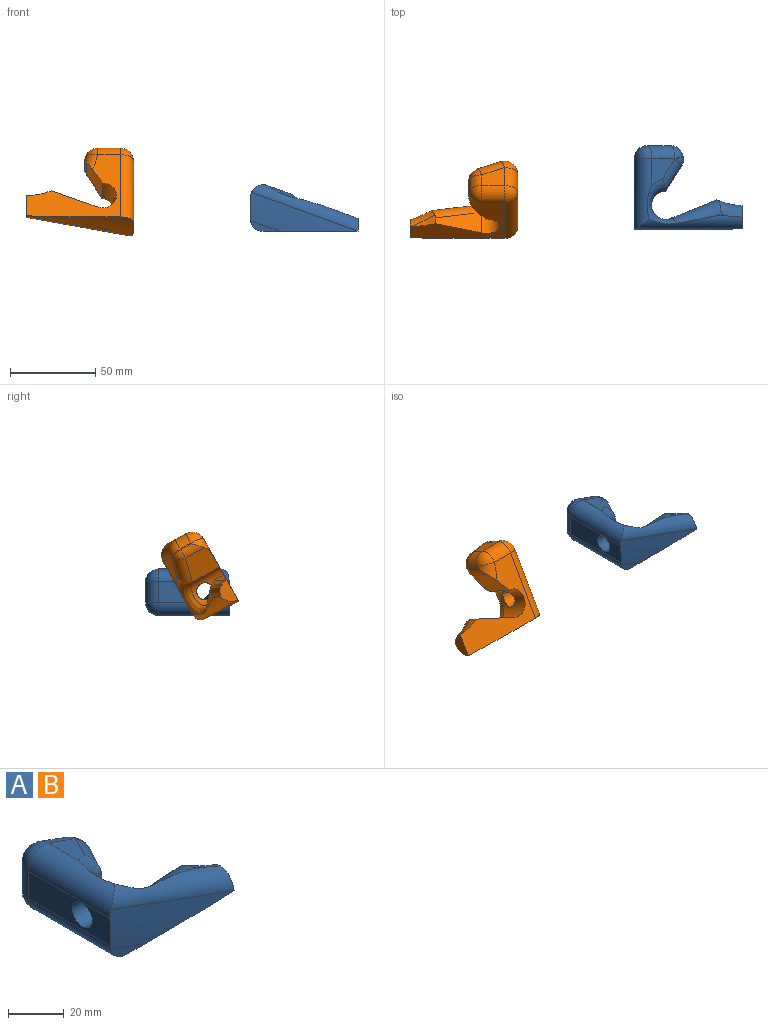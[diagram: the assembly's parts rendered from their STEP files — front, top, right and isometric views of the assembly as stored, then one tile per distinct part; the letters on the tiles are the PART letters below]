
ASSEMBLY  parts=2 mates=2
PART A: 33 faces, bbox 71.2x51.8x45.1 mm
  f0: plane 6.02x2.19mm, normal (0.34,0,0.94), area 3.4mm2, adj f30,f31,f32
  f1: plane 15.57x13.56mm, normal (0.34,0,0.94), area 138.2mm2, adj f21,f24,f27,f28,f29
  f2: plane 14.53x8.49mm, normal (1,0,0), area 77.7mm2, adj f3,f13,f31,f32
  f3: plane 55.6x41.91mm, normal (0,0,-1), area 972.8mm2, adj f2,f5,f6,f7,f8,f9,f13,f15
  f4: plane 41.86x12.11mm, normal (-1,0,0), area 424.4mm2, adj f12,f13,f15,f23,f28
  f5: plane 17.37x6.32mm, normal (0,-1,0), area 43.2mm2, adj f3,f13,f15
  f6: cylinder r=35.16mm len=13.75mm, axis (0,0,-1), area 43mm2, adj f3,f7,f30,f31
  f7: plane 26.86x13.66mm, normal (-0.37,0.93,0), area 254mm2, adj f3,f6,f8,f30
  f8: cylinder r=8.32mm len=21.65mm, axis (0,0,-1), area 472.5mm2, adj f3,f7,f9,f12,f29
  f9: plane 18.21x14.52mm, normal (0.84,-0.54,0), area 277.7mm2, adj f3,f8,f18,f22,f27,f29
  f10: cylinder r=35.16mm len=7.21mm, axis (0,0,-1), area 3.2mm2, adj f17,f18,f21,f22
  f11: plane 13.46x12.11mm, normal (0,1,0), area 130mm2, adj f16,f17,f23,f24
  f12: cylinder r=5.07mm len=10.14mm, axis (-1,0,0), area 319.1mm2, adj f4,f8
  f13: cylinder r=177.8mm len=67.98mm, axis (-0.94,0,0.34), area 685.5mm2, adj f2,f3,f4,f5,f15,f28,f32
  f14: sphere r=7.62mm, area 51.4mm2, adj f16,f17,f18
  f15: cylinder r=7.62mm len=41.87mm, axis (0,-1,0), area 501.1mm2, adj f3,f4,f5,f13,f19
  f16: cylinder r=7.62mm len=13.46mm, axis (-1,0,0), area 161.1mm2, adj f3,f11,f14,f19
  f17: cylinder r=7.62mm len=7.5mm, axis (0,0,-1), area 76.5mm2, adj f10,f11,f14,f20
  f18: torus R=42.78mm, axis (0,0,1), area 65.5mm2, adj f3,f9,f10,f14,f22
  f19: sphere r=7.62mm, area 124.4mm2, adj f15,f16,f23
  f20: sphere r=7.62mm, area 41.6mm2, adj f17,f21,f24
  f21: bspline ~7.2x4.97mm, area 4.6mm2, adj f1,f10,f20,f25
  f22: cylinder r=7.62mm len=12.8mm, axis (0,0,-1), area 58mm2, adj f9,f10,f18,f25
  f23: cylinder r=7.62mm len=12.11mm, axis (0,0,-1), area 145mm2, adj f4,f11,f19,f26
  f24: cylinder r=7.62mm len=16.06mm, axis (0.94,0,-0.34), area 171.4mm2, adj f1,f11,f20,f26
  f25: sphere r=7.62mm, area 23.8mm2, adj f21,f22,f27
  f26: sphere r=7.62mm, area 111.5mm2, adj f23,f24,f28
  f27: cylinder r=7.62mm len=18.21mm, axis (-0.53,-0.83,0.19), area 151.5mm2, adj f1,f9,f25,f29
  f28: cylinder r=7.62mm len=41.42mm, axis (0,1,0), area 523mm2, adj f1,f4,f13,f26,f29,f32
  f29: bspline ~31.88x21.91mm, area 293.1mm2, adj f1,f8,f9,f27,f28,f30,f32
  f30: cylinder r=7.62mm len=32.32mm, axis (0.88,0.35,-0.32), area 317.8mm2, adj f0,f6,f7,f29,f31,f32
  f31: bspline ~17.47x13.52mm, area 157.8mm2, adj f0,f2,f3,f6,f30,f32
  f32: cylinder r=7.62mm len=64.83mm, axis (-0.94,0,0.34), area 559.1mm2, adj f0,f2,f13,f28,f29,f30,f31
PART B: same geometry as A
PLACE A t=(-94.36,-29.24,41.28)mm fixed
PLACE B rot(axis=(0,-0.86,-0.5),180deg) t=(-162.88,-27.59,38.46)mm
MATE cylindrical B.f12 <-> A.f12  axis (1,0,0) through (-162.88,-14.78,47.84)mm
MATE parallel B.f4 <-> A.f4  axis (1,0,0) through (-162.88,-11.48,54.94)mm
